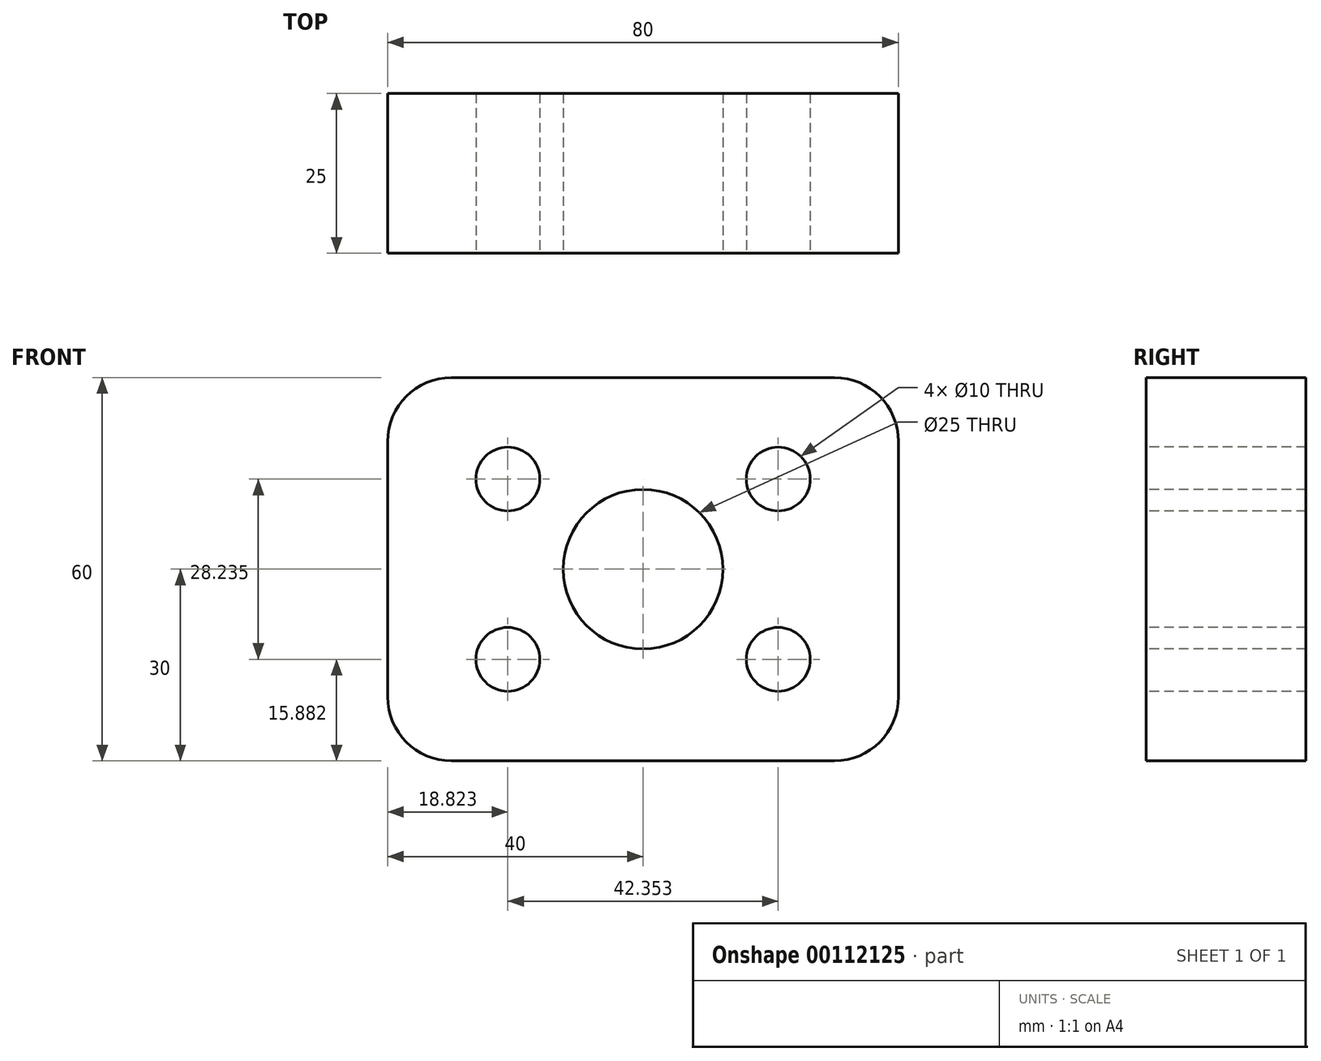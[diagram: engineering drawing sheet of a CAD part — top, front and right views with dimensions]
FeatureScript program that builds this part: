
annotation { "Feature Type Name" : "Feature", "Feature Type Description" : "" }
export const myFeature = defineFeature(function(context is Context, id is Id, definition is map)
    precondition{}
    {
        {
            var Q0;
            Q0=qCreatedBy(makeId("Front.planeOp"),FACE);
            var sketch = newSketch(context, id + "F0", { "sketchPlane" : qUnion([Q0])});
            skLineSegment(sketch, "E0", {"start": v(40, -30) * mm, "end": v(40, 30) * mm});
            skLineSegment(sketch, "E1", {"start": v(40, 30) * mm, "end": v(-40, 30) * mm});
            skLineSegment(sketch, "E2", {"start": v(-40, 30) * mm, "end": v(-40, -30) * mm});
            skLineSegment(sketch, "E3", {"start": v(-40, -30) * mm, "end": v(40, -30) * mm});
            skSolve(sketch);
        }
        {
            var Q0;
            Q0 = qSketchRegion(id + "F0", true);
            extrude(context, id + "F1", {"entities" : qUnion([Q0]), "endBound" : BoundingType.SYMMETRIC, "depth" : 25 * mm});
        }
        {
            var Q0;
            Q0=makeQuery(id+"F1.opExtrude","CAP_FACE",FACE,{"disambiguationData":[OSD([sQuery(id+"F0.wireOp",EDGE,"E0"),sQuery(id+"F0.wireOp",EDGE,"E1"),sQuery(id+"F0.wireOp",EDGE,"E2"),sQuery(id+"F0.wireOp",EDGE,"E3")])],"isStart":false});
            var sketch = newSketch(context, id + "F2", { "sketchPlane" : qUnion([Q0])});
            skCircle(sketch, "E4", {"center": v(0, 0) * mm, "radius": 12.5 * mm});
            skSolve(sketch);
        }
        {
            var Q0;
            Q0 = qSketchRegion(id + "F2", true);
            extrude(context, id + "F3", {"entities" : qUnion([Q0]), "operationType" : NewBodyOperationType.REMOVE, "endBound" : BoundingType.UP_TO_NEXT, "oppositeDirection" : true, "depth" : 25 * mm});
        }
        {
            var Q0;
            Q0=makeQuery(id+"F1.opExtrude","SWEPT_EDGE",EDGE,{"disambiguationData":[OSD([sQuery(id+"F0.wireOp",EDGE,"E1"),sQuery(id+"F0.wireOp",EDGE,"E2")])]});
            var Q1;
            Q1=makeQuery(id+"F1.opExtrude","SWEPT_EDGE",EDGE,{"disambiguationData":[OSD([sQuery(id+"F0.wireOp",EDGE,"E0"),sQuery(id+"F0.wireOp",EDGE,"E1")])]});
            var Q2;
            Q2=makeQuery(id+"F1.opExtrude","SWEPT_EDGE",EDGE,{"disambiguationData":[OSD([sQuery(id+"F0.wireOp",EDGE,"E0"),sQuery(id+"F0.wireOp",EDGE,"E3")])]});
            var Q3;
            Q3=makeQuery(id+"F1.opExtrude","SWEPT_EDGE",EDGE,{"disambiguationData":[OSD([sQuery(id+"F0.wireOp",EDGE,"E2"),sQuery(id+"F0.wireOp",EDGE,"E3")])]});
            fillet(context, id + "F4", {"entities" : qUnion([Q0, Q1, Q2, Q3]), "radius" : 10 * mm, "tangentPropagation" : true, "allowEdgeOverflow" : false});
        }
        {
            var Q0;
            Q0=makeQuery(id+"F1.opExtrude","CAP_FACE",FACE,{"disambiguationData":[OSD([sQuery(id+"F0.wireOp",EDGE,"E0"),sQuery(id+"F0.wireOp",EDGE,"E1"),sQuery(id+"F0.wireOp",EDGE,"E2"),sQuery(id+"F0.wireOp",EDGE,"E3")])],"isStart":false});
            var sketch = newSketch(context, id + "F5", { "sketchPlane" : qUnion([Q0])});
            skCircle(sketch, "E5", {"center": v(-21.18, 14.12) * mm, "radius": 5 * mm});
            skCircle(sketch, "E6.MirrorC", {"center": v(21.18, 14.12) * mm, "radius": 5 * mm});
            skCircle(sketch, "E7.MirrorC", {"center": v(-21.18, -14.12) * mm, "radius": 5 * mm});
            skCircle(sketch, "E8.MirrorC", {"center": v(21.18, -14.12) * mm, "radius": 5 * mm});
            skSolve(sketch);
        }
        {
            var Q0;
            Q0=sQuery(id+"F5.wireOp",VERTEX,"E5.center");
            var Q1;
            Q1=sQuery(id+"F5.wireOp",VERTEX,"E7.MirrorC.center");
            var Q2;
            Q2=sQuery(id+"F5.wireOp",VERTEX,"E6.MirrorC.center");
            var Q3;
            Q3=sQuery(id+"F5.wireOp",VERTEX,"E8.MirrorC.center");
            var Q4;
            Q4=makeQuery(id+"F1.opExtrude","SWEPT_BODY",BODY,{"disambiguationData":[OSD([sQuery(id+"F0.wireOp",EDGE,"E0"),sQuery(id+"F0.wireOp",EDGE,"E1"),sQuery(id+"F0.wireOp",EDGE,"E2"),sQuery(id+"F0.wireOp",EDGE,"E3")])]});
            hole(context, id + "F6", {"style" : HoleStyle.SIMPLE, "endStyle" : HoleEndStyle.THROUGH, "holeDiameter" : 10 * mm, "locations" : qUnion([Q0, Q1, Q2, Q3]), "scope" : qUnion([Q4]), "isTappedThrough" : true});
        }
    });
